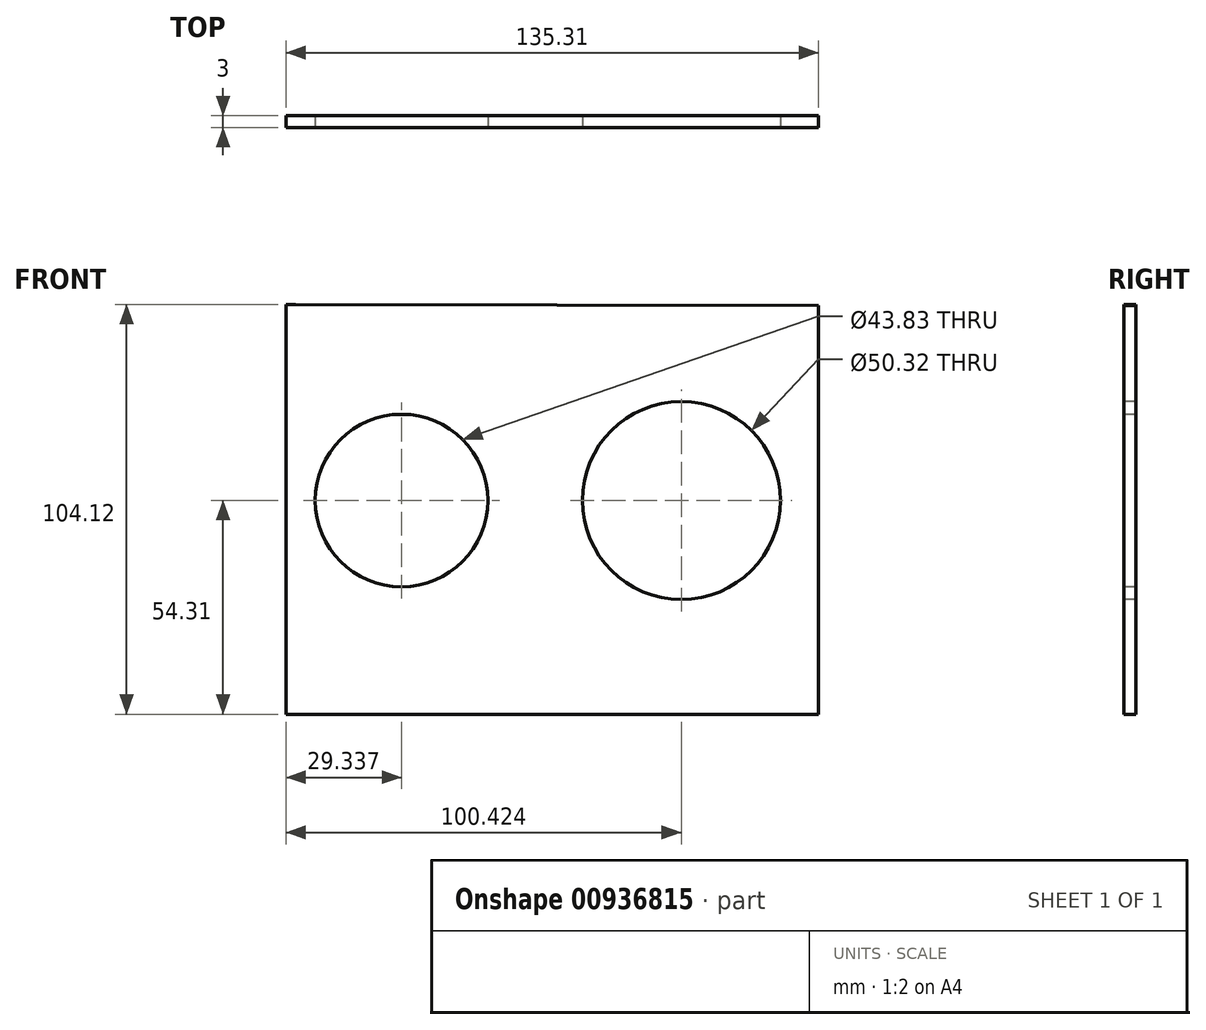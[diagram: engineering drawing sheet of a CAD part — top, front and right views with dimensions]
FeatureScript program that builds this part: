
annotation { "Feature Type Name" : "Feature", "Feature Type Description" : "" }
export const myFeature = defineFeature(function(context is Context, id is Id, definition is map)
    precondition{}
    {
        {
            var Q0;
            Q0=qCreatedBy(makeId("Front.planeOp"),FACE);
            var sketch = newSketch(context, id + "F0", { "sketchPlane" : qUnion([Q0])});
            skLineSegment(sketch, "E0", {"start": v(-70.43, 49.81) * mm, "end": v(-70.43, -54.3) * mm});
            skLineSegment(sketch, "E1", {"start": v(-70.43, -54.3) * mm, "end": v(64.88, -54.3) * mm});
            skLineSegment(sketch, "E2", {"start": v(64.88, -54.3) * mm, "end": v(64.88, 49.55) * mm});
            skLineSegment(sketch, "E3", {"start": v(-68.05, 49.81) * mm, "end": v(-70.43, 49.81) * mm});
            skLineSegment(sketch, "E4", {"start": v(-68.05, 49.81) * mm, "end": v(64.88, 49.55) * mm});
            skCircle(sketch, "E5", {"center": v(-41.1, 0) * mm, "radius": 21.91 * mm});
            skCircle(sketch, "E6", {"center": v(30, 0) * mm, "radius": 25.16 * mm});
            skSolve(sketch);
        }
        {
            var Q0;
            Q0 = qSketchRegion(id + "F0", true);
            extrude(context, id + "F1", {"entities" : qUnion([Q0]), "oppositeDirection" : true, "depth" : 3 * mm, "offsetDistance" : 25 * mm});
        }
    });
